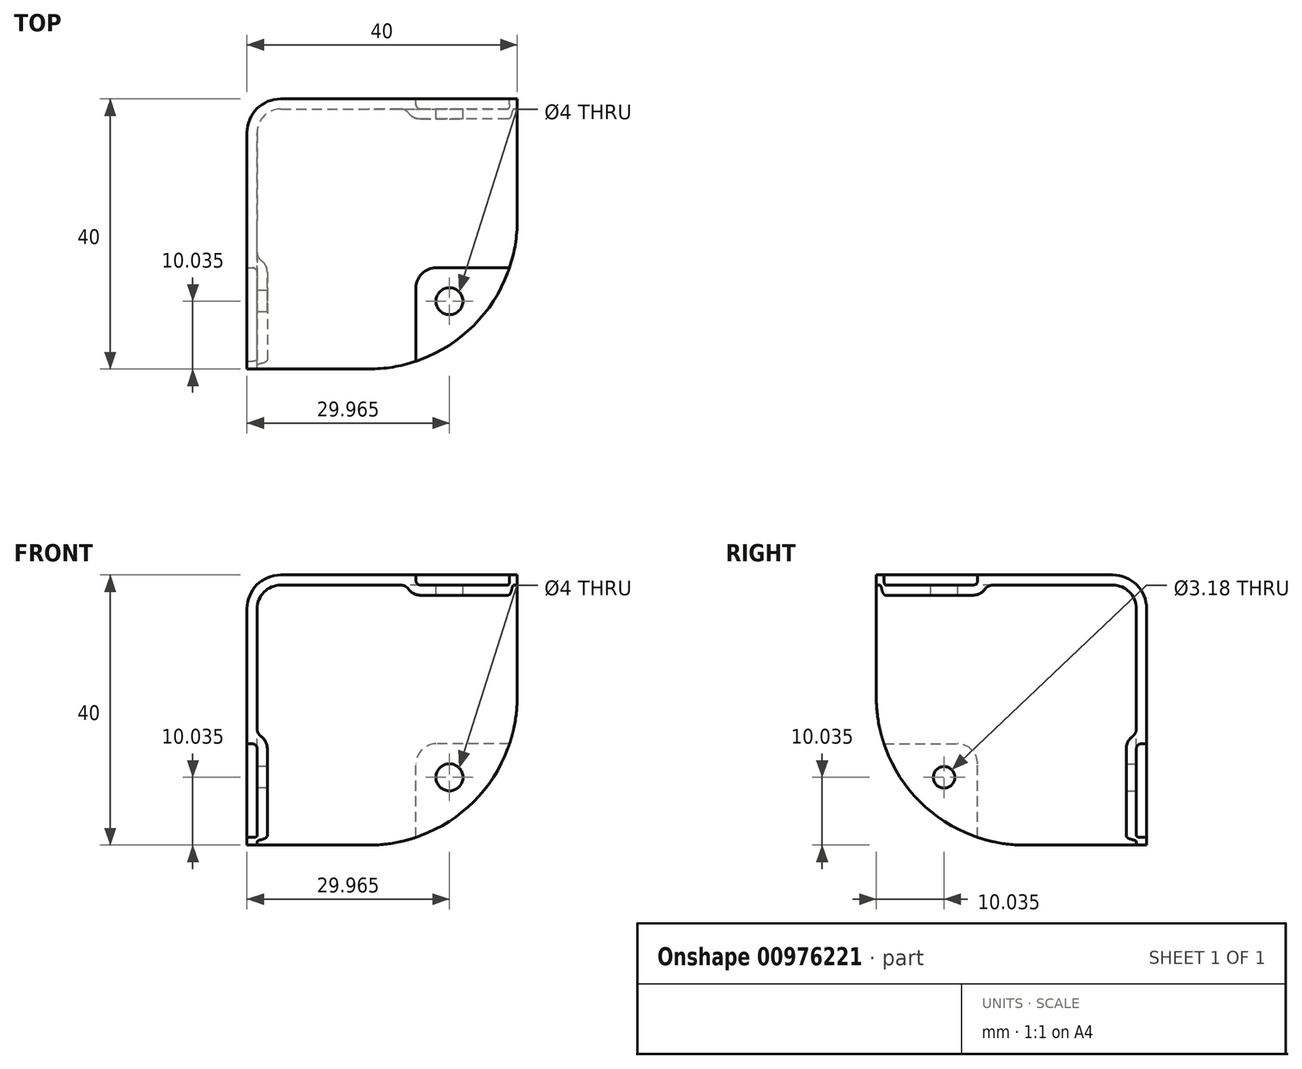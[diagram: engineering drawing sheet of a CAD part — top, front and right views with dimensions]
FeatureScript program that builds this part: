
annotation { "Feature Type Name" : "Feature", "Feature Type Description" : "" }
export const myFeature = defineFeature(function(context is Context, id is Id, definition is map)
    precondition{}
    {
        {
            var Q0;
            Q0=qCreatedBy(makeId("Top.planeOp"),FACE);
            var sketch = newSketch(context, id + "F0", { "sketchPlane" : qUnion([Q0])});
            skLineSegment(sketch, "E0.bottom", {"start": v(0, 0) * mm, "end": v(40, 0) * mm});
            skLineSegment(sketch, "E0.top", {"start": v(0, -40) * mm, "end": v(40, -40) * mm});
            skLineSegment(sketch, "E0.left", {"start": v(0, 0) * mm, "end": v(0, -40) * mm});
            skLineSegment(sketch, "E0.right", {"start": v(40, 0) * mm, "end": v(40, -40) * mm});
            skSolve(sketch);
        }
        {
            var Q0;
            Q0 = qSketchRegion(id + "F0", true);
            extrude(context, id + "F1", {"entities" : qUnion([Q0]), "depth" : 40 * mm, "offsetDistance" : 25 * mm});
        }
        {
            var Q0;
            Q0=makeQuery(id+"F1.opExtrude","SWEPT_EDGE",EDGE,{"disambiguationData":[OSD([sQuery(id+"F0.wireOp",EDGE,"E0.bottom"),sQuery(id+"F0.wireOp",EDGE,"E0.left")])]});
            var Q1;
            Q1=makeQuery(id+"F1.opExtrude","CAP_EDGE",EDGE,{"disambiguationData":[OSD([sQuery(id+"F0.wireOp",EDGE,"E0.left")])],"isStart":false});
            var Q2;
            Q2=makeQuery(id+"F1.opExtrude","CAP_EDGE",EDGE,{"disambiguationData":[OSD([sQuery(id+"F0.wireOp",EDGE,"E0.bottom")])],"isStart":false});
            fillet(context, id + "F2", {"entities" : qUnion([Q0, Q1, Q2]), "radius" : 5 * mm, "tangentPropagation" : true, "allowEdgeOverflow" : false});
        }
        {
            var Q0;
            Q0=makeQuery(id+"F1.opExtrude","CAP_FACE",FACE,{"disambiguationData":[OSD([sQuery(id+"F0.wireOp",EDGE,"E0.bottom"),sQuery(id+"F0.wireOp",EDGE,"E0.top"),sQuery(id+"F0.wireOp",EDGE,"E0.left"),sQuery(id+"F0.wireOp",EDGE,"E0.right")])],"isStart":false});
            var sketch = newSketch(context, id + "F3", { "sketchPlane" : qUnion([Q0])});
            skLineSegment(sketch, "E1.bottom", {"start": v(40, -40) * mm, "end": v(25, -40) * mm});
            skLineSegment(sketch, "E1.top", {"start": v(40, -25) * mm, "end": v(25, -25) * mm});
            skLineSegment(sketch, "E1.left", {"start": v(40, -40) * mm, "end": v(40, -25) * mm});
            skLineSegment(sketch, "E1.right", {"start": v(25, -40) * mm, "end": v(25, -25) * mm});
            skSolve(sketch);
        }
        {
            var Q0;
            Q0=makeQuery(id+"F1.opExtrude","SWEPT_FACE",FACE,{"disambiguationData":[OSD([sQuery(id+"F0.wireOp",EDGE,"E0.bottom")])]});
            var sketch = newSketch(context, id + "F4", { "sketchPlane" : qUnion([Q0])});
            skLineSegment(sketch, "E2.bottom", {"start": v(-40, 0) * mm, "end": v(-25, 0) * mm});
            skLineSegment(sketch, "E2.top", {"start": v(-40, 15) * mm, "end": v(-25, 15) * mm});
            skLineSegment(sketch, "E2.left", {"start": v(-40, 0) * mm, "end": v(-40, 15) * mm});
            skLineSegment(sketch, "E2.right", {"start": v(-25, 0) * mm, "end": v(-25, 15) * mm});
            skSolve(sketch);
        }
        {
            var Q0;
            Q0=makeQuery(id+"F1.opExtrude","SWEPT_FACE",FACE,{"disambiguationData":[OSD([sQuery(id+"F0.wireOp",EDGE,"E0.left")])]});
            var sketch = newSketch(context, id + "F5", { "sketchPlane" : qUnion([Q0])});
            skLineSegment(sketch, "E3.bottom", {"start": v(40, 0) * mm, "end": v(25, 0) * mm});
            skLineSegment(sketch, "E3.top", {"start": v(40, 15) * mm, "end": v(25, 15) * mm});
            skLineSegment(sketch, "E3.left", {"start": v(40, 0) * mm, "end": v(40, 15) * mm});
            skLineSegment(sketch, "E3.right", {"start": v(25, 0) * mm, "end": v(25, 15) * mm});
            skSolve(sketch);
        }
        {
            var Q0;
            Q0=makeQuery(id+"F3.imprint","IMPRINT",FACE,{"disambiguationData":[TD([[makeQuery(id+"F3.imprint","IMPRINT",EDGE,{"derivedFrom":sQuery(id+"F3.wireOp",EDGE,"E1.bottom")}),1.0]])]});
            extrude(context, id + "F6", {"entities" : qUnion([Q0]), "operationType" : NewBodyOperationType.REMOVE, "oppositeDirection" : true, "depth" : 1.5 * mm, "offsetDistance" : 25 * mm});
        }
        {
            var Q0;
            Q0 = qSketchRegion(id + "F5", true);
            extrude(context, id + "F7", {"entities" : qUnion([Q0]), "operationType" : NewBodyOperationType.REMOVE, "oppositeDirection" : true, "depth" : 1.5 * mm, "offsetDistance" : 25 * mm});
        }
        {
            var Q0;
            Q0 = qSketchRegion(id + "F4", true);
            extrude(context, id + "F8", {"entities" : qUnion([Q0]), "operationType" : NewBodyOperationType.REMOVE, "oppositeDirection" : true, "depth" : 1.5 * mm, "offsetDistance" : 25 * mm});
        }
        {
            var Q0;
            Q0=makeQuery(id+"F6.boolean.opBoolean","COPY",EDGE,{"derivedFrom":makeQuery(id+"F6.opExtrude","SWEPT_EDGE",EDGE,{"disambiguationData":[OSD([sQuery(id+"F3.wireOp",EDGE,"E1.top"),sQuery(id+"F3.wireOp",EDGE,"E1.right")])]})});
            var Q1;
            Q1=makeQuery(id+"F8.boolean.opBoolean","COPY",EDGE,{"derivedFrom":makeQuery(id+"F8.opExtrude","SWEPT_EDGE",EDGE,{"disambiguationData":[OSD([sQuery(id+"F4.wireOp",EDGE,"E2.top"),sQuery(id+"F4.wireOp",EDGE,"E2.right")])]})});
            var Q2;
            Q2=makeQuery(id+"F7.boolean.opBoolean","COPY",EDGE,{"derivedFrom":makeQuery(id+"F7.opExtrude","SWEPT_EDGE",EDGE,{"disambiguationData":[OSD([sQuery(id+"F5.wireOp",EDGE,"E3.top"),sQuery(id+"F5.wireOp",EDGE,"E3.right")])]})});
            fillet(context, id + "F9", {"entities" : qUnion([Q0, Q1, Q2]), "radius" : 3 * mm, "tangentPropagation" : true, "allowEdgeOverflow" : false});
        }
        {
            var Q0;
            Q0=makeQuery(id+"F6.boolean.opBoolean","COPY",EDGE,{"derivedFrom":makeQuery(id+"F6.opExtrude","CAP_EDGE",EDGE,{"disambiguationData":[OSD([sQuery(id+"F3.wireOp",EDGE,"E1.top")])],"isStart":true})});
            var Q1;
            Q1=makeQuery(id+"F6.boolean.opBoolean","COPY",EDGE,{"derivedFrom":makeQuery(id+"F6.opExtrude","CAP_EDGE",EDGE,{"disambiguationData":[OSD([sQuery(id+"F3.wireOp",EDGE,"E1.top")])],"isStart":false})});
            var Q2;
            Q2=makeQuery(id+"F6.boolean.opBoolean","COPY",EDGE,{"derivedFrom":makeQuery(id+"F6.opExtrude","CAP_EDGE",EDGE,{"disambiguationData":[OSD([sQuery(id+"F3.wireOp",EDGE,"E1.right")])],"isStart":false})});
            var Q3;
            Q3=makeQuery(id+"F6.boolean.opBoolean","COPY",EDGE,{"derivedFrom":makeQuery(id+"F6.opExtrude","CAP_EDGE",EDGE,{"disambiguationData":[OSD([sQuery(id+"F3.wireOp",EDGE,"E1.right")])],"isStart":true})});
            var Q4;
            Q4=makeQuery(id+"F7.boolean.opBoolean","COPY",EDGE,{"derivedFrom":makeQuery(id+"F7.opExtrude","CAP_EDGE",EDGE,{"disambiguationData":[OSD([sQuery(id+"F5.wireOp",EDGE,"E3.top")])],"isStart":true})});
            var Q5;
            Q5=makeQuery(id+"F7.boolean.opBoolean","COPY",EDGE,{"derivedFrom":makeQuery(id+"F7.opExtrude","CAP_EDGE",EDGE,{"disambiguationData":[OSD([sQuery(id+"F5.wireOp",EDGE,"E3.top")])],"isStart":false})});
            var Q6;
            Q6=makeQuery(id+"F8.boolean.opBoolean","COPY",EDGE,{"derivedFrom":makeQuery(id+"F8.opExtrude","CAP_EDGE",EDGE,{"disambiguationData":[OSD([sQuery(id+"F4.wireOp",EDGE,"E2.top")])],"isStart":false})});
            var Q7;
            Q7=makeQuery(id+"F8.boolean.opBoolean","COPY",EDGE,{"derivedFrom":makeQuery(id+"F8.opExtrude","CAP_EDGE",EDGE,{"disambiguationData":[OSD([sQuery(id+"F4.wireOp",EDGE,"E2.top")])],"isStart":true})});
            fillet(context, id + "F10", {"entities" : qUnion([Q0, Q1, Q2, Q3, Q4, Q5, Q6, Q7]), "radius" : 0.7 * mm, "tangentPropagation" : true, "allowEdgeOverflow" : false});
        }
        {
            var Q0;
            Q0=makeQuery(id+"F1.opExtrude","CAP_EDGE",EDGE,{"disambiguationData":[OSD([sQuery(id+"F0.wireOp",EDGE,"E0.right")])],"isStart":true});
            var Q1;
            Q1=makeQuery(id+"F1.opExtrude","CAP_EDGE",EDGE,{"disambiguationData":[OSD([sQuery(id+"F0.wireOp",EDGE,"E0.top")])],"isStart":true});
            var Q2;
            Q2=makeQuery(id+"F1.opExtrude","SWEPT_EDGE",EDGE,{"disambiguationData":[OSD([sQuery(id+"F0.wireOp",EDGE,"E0.top"),sQuery(id+"F0.wireOp",EDGE,"E0.right")])]});
            fillet(context, id + "F11", {"entities" : qUnion([Q0, Q1, Q2]), "radius" : 22 * mm, "tangentPropagation" : true, "allowEdgeOverflow" : false});
        }
        {
            var Q0;
            Q0=makeQuery(id+"F11.opFillet","BLEND_FACE",FACE,{"disambiguationData":[OSD([sQuery(id+"F0.wireOp",EDGE,"E0.right")])]});
            var Q1;
            {var subQ0=sQuery(id+"F0.wireOp",EDGE,"E0.right");var subQ1=sQuery(id+"F0.wireOp",EDGE,"E0.top");Q1=makeQuery(id+"F11.opFillet","BLEND_FACE",FACE,{"disambiguationData":[OSD([subQ1,subQ0]),TDD([makeQuery(id+"F1.opExtrude","CAP_VERTEX",VERTEX,{"disambiguationData":[OSD([subQ1,subQ0])],"isStart":true})])]});}
            var Q2;
            Q2=makeQuery(id+"F11.opFillet","BLEND_FACE",FACE,{"disambiguationData":[OSD([sQuery(id+"F0.wireOp",EDGE,"E0.top")])]});
            var Q3;
            Q3=makeQuery(id+"F1.opExtrude","CAP_FACE",FACE,{"disambiguationData":[OSD([sQuery(id+"F0.wireOp",EDGE,"E0.bottom"),sQuery(id+"F0.wireOp",EDGE,"E0.top"),sQuery(id+"F0.wireOp",EDGE,"E0.left"),sQuery(id+"F0.wireOp",EDGE,"E0.right")])],"isStart":true});
            var Q4;
            {var subQ0=sQuery(id+"F0.wireOp",EDGE,"E0.right");var subQ1=sQuery(id+"F0.wireOp",EDGE,"E0.top");Q4=makeQuery(id+"F11.opFillet","BLEND_FACE",FACE,{"disambiguationData":[OSD([subQ1,subQ0]),TDD([makeQuery(id+"F1.opExtrude","SWEPT_EDGE",EDGE,{"disambiguationData":[OSD([subQ1,subQ0])]})])]});}
            var Q5;
            Q5=makeQuery(id+"F1.opExtrude","SWEPT_FACE",FACE,{"disambiguationData":[OSD([sQuery(id+"F0.wireOp",EDGE,"E0.right")])]});
            var Q6;
            Q6=makeQuery(id+"F1.opExtrude","SWEPT_FACE",FACE,{"disambiguationData":[OSD([sQuery(id+"F0.wireOp",EDGE,"E0.top")])]});
            shell(context, id + "F12", {"entities" : qUnion([Q0, Q1, Q2, Q3, Q4, Q5, Q6]), "thickness" : 1.5 * mm});
        }
        {
            var Q0;
            {var subQ0=sQuery(id+"F5.wireOp",EDGE,"E3.right");Q0=makeQuery(id+"F12.opShell","TWEAK_EDGE",EDGE,{"derivedFrom":[makeQuery(id+"F10.opFillet","BLEND_FACE",FACE,{"disambiguationData":[OSD([subQ0]),TDD([makeQuery(id+"F7.boolean.opBoolean","COPY",EDGE,{"derivedFrom":makeQuery(id+"F7.opExtrude","CAP_EDGE",EDGE,{"disambiguationData":[OSD([subQ0])],"isStart":false})})])]}),makeQuery(id+"F1.opExtrude","SWEPT_FACE",FACE,{"disambiguationData":[OSD([sQuery(id+"F0.wireOp",EDGE,"E0.left")])]})]});}
            var Q1;
            {var subQ0=sQuery(id+"F3.wireOp",EDGE,"E1.right");Q1=makeQuery(id+"F12.opShell","TWEAK_EDGE",EDGE,{"derivedFrom":[makeQuery(id+"F10.opFillet","BLEND_FACE",FACE,{"disambiguationData":[OSD([subQ0]),TDD([makeQuery(id+"F6.boolean.opBoolean","COPY",EDGE,{"derivedFrom":makeQuery(id+"F6.opExtrude","CAP_EDGE",EDGE,{"disambiguationData":[OSD([subQ0])],"isStart":false})})])]}),makeQuery(id+"F1.opExtrude","CAP_FACE",FACE,{"disambiguationData":[OSD([sQuery(id+"F0.wireOp",EDGE,"E0.bottom"),sQuery(id+"F0.wireOp",EDGE,"E0.top"),sQuery(id+"F0.wireOp",EDGE,"E0.left"),sQuery(id+"F0.wireOp",EDGE,"E0.right")])],"isStart":false})]});}
            var Q2;
            {var subQ0=sQuery(id+"F4.wireOp",EDGE,"E2.right");Q2=makeQuery(id+"F12.opShell","TWEAK_EDGE",EDGE,{"derivedFrom":[makeQuery(id+"F10.opFillet","BLEND_FACE",FACE,{"disambiguationData":[OSD([subQ0]),TDD([makeQuery(id+"F8.boolean.opBoolean","COPY",EDGE,{"derivedFrom":makeQuery(id+"F8.opExtrude","CAP_EDGE",EDGE,{"disambiguationData":[OSD([subQ0])],"isStart":false})})])]}),makeQuery(id+"F1.opExtrude","SWEPT_FACE",FACE,{"disambiguationData":[OSD([sQuery(id+"F0.wireOp",EDGE,"E0.bottom")])]})]});}
            fillet(context, id + "F13", {"entities" : qUnion([Q0, Q1, Q2]), "radius" : 1.5 * mm, "tangentPropagation" : true, "allowEdgeOverflow" : false});
        }
        {
            var Q0;
            Q0=makeQuery(id+"F6.boolean.opBoolean","COPY",FACE,{"derivedFrom":makeQuery(id+"F6.opExtrude","CAP_FACE",FACE,{"disambiguationData":[OSD([sQuery(id+"F3.wireOp",EDGE,"E1.bottom"),sQuery(id+"F3.wireOp",EDGE,"E1.top"),sQuery(id+"F3.wireOp",EDGE,"E1.left"),sQuery(id+"F3.wireOp",EDGE,"E1.right")])],"isStart":false})});
            var sketch = newSketch(context, id + "F14", { "sketchPlane" : qUnion([Q0])});
            skLineSegment(sketch, "E4", {"start": v(26.37, -26.37) * mm, "end": v(33.56, -33.56) * mm, "construction": true});
            skCircle(sketch, "E5", {"center": v(29.97, -29.97) * mm, "radius": 2 * mm});
            skSolve(sketch);
        }
        {
            var Q0;
            Q0 = qSketchRegion(id + "F14", true);
            extrude(context, id + "F15", {"entities" : qUnion([Q0]), "operationType" : NewBodyOperationType.REMOVE, "oppositeDirection" : true, "depth" : 25 * mm, "offsetDistance" : 25 * mm});
        }
        {
            var Q0;
            Q0=makeQuery(id+"F7.boolean.opBoolean","COPY",FACE,{"derivedFrom":makeQuery(id+"F7.opExtrude","CAP_FACE",FACE,{"disambiguationData":[OSD([sQuery(id+"F5.wireOp",EDGE,"E3.bottom"),sQuery(id+"F5.wireOp",EDGE,"E3.top"),sQuery(id+"F5.wireOp",EDGE,"E3.left"),sQuery(id+"F5.wireOp",EDGE,"E3.right")])],"isStart":false})});
            var sketch = newSketch(context, id + "F16", { "sketchPlane" : qUnion([Q0])});
            skLineSegment(sketch, "E6", {"start": v(33.56, 6.44) * mm, "end": v(26.37, 13.63) * mm, "construction": true});
            skCircle(sketch, "E7", {"center": v(29.97, 10.03) * mm, "radius": 1.6 * mm});
            skSolve(sketch);
        }
        {
            var Q0;
            Q0 = qSketchRegion(id + "F16", true);
            extrude(context, id + "F17", {"entities" : qUnion([Q0]), "operationType" : NewBodyOperationType.REMOVE, "oppositeDirection" : true, "depth" : 25 * mm, "offsetDistance" : 25 * mm});
        }
        {
            var Q0;
            Q0=makeQuery(id+"F8.boolean.opBoolean","COPY",FACE,{"derivedFrom":makeQuery(id+"F8.opExtrude","CAP_FACE",FACE,{"disambiguationData":[OSD([sQuery(id+"F4.wireOp",EDGE,"E2.bottom"),sQuery(id+"F4.wireOp",EDGE,"E2.top"),sQuery(id+"F4.wireOp",EDGE,"E2.left"),sQuery(id+"F4.wireOp",EDGE,"E2.right")])],"isStart":false})});
            var sketch = newSketch(context, id + "F18", { "sketchPlane" : qUnion([Q0])});
            skLineSegment(sketch, "E8", {"start": v(-26.37, 13.63) * mm, "end": v(-33.56, 6.44) * mm, "construction": true});
            skCircle(sketch, "E9", {"center": v(-29.97, 10.03) * mm, "radius": 2 * mm});
            skSolve(sketch);
        }
        {
            var Q0;
            Q0 = qSketchRegion(id + "F18", true);
            extrude(context, id + "F19", {"entities" : qUnion([Q0]), "operationType" : NewBodyOperationType.REMOVE, "oppositeDirection" : true, "depth" : 25 * mm, "offsetDistance" : 25 * mm});
        }
    });
